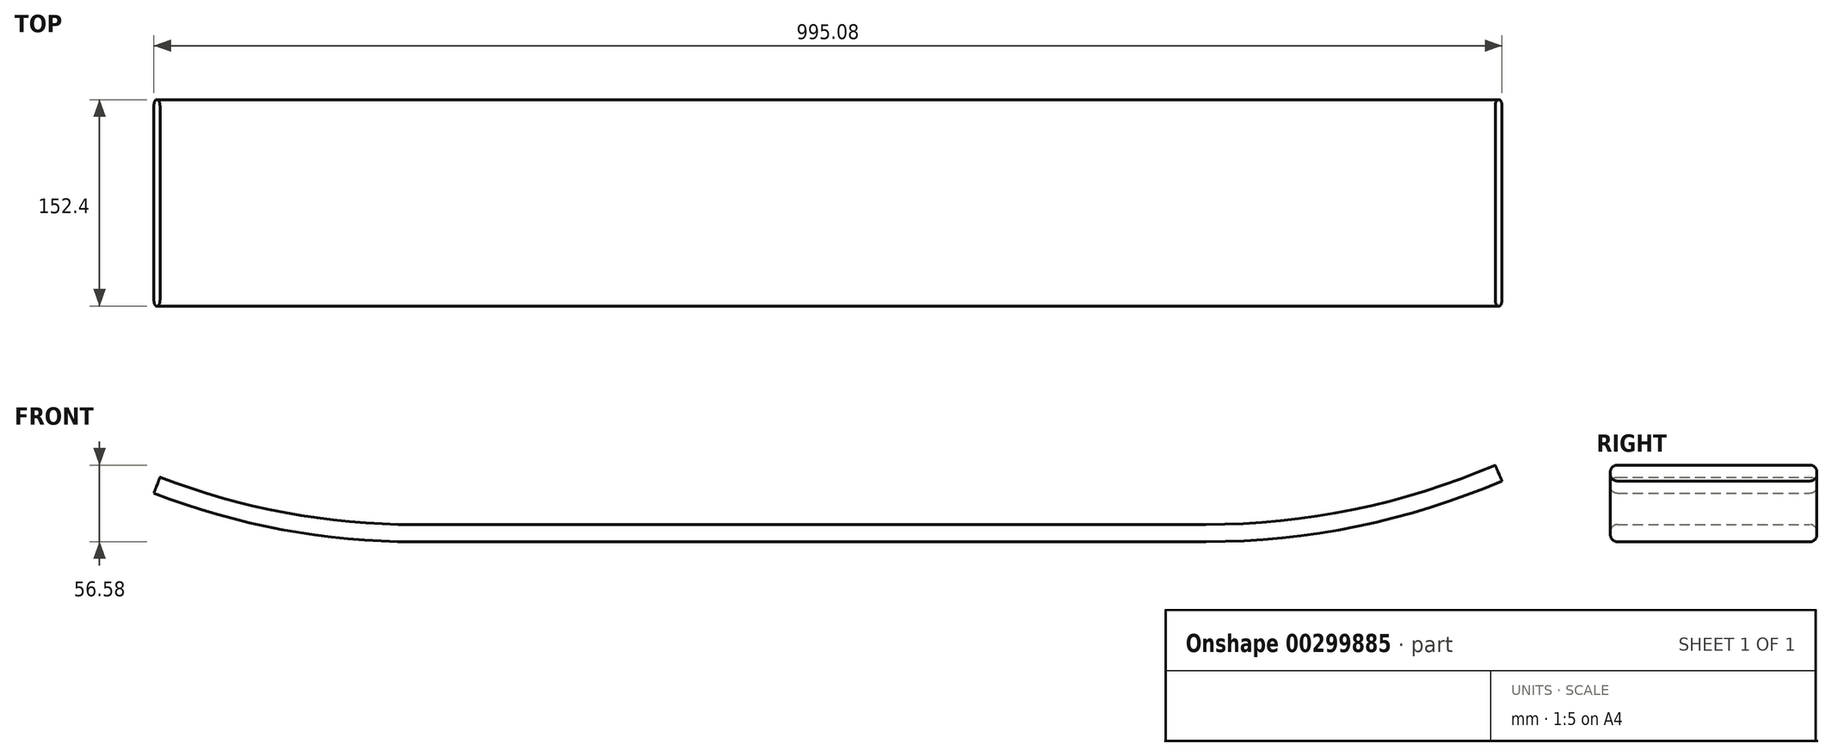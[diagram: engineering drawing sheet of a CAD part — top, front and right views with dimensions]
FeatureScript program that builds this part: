
annotation { "Feature Type Name" : "Feature", "Feature Type Description" : "" }
export const myFeature = defineFeature(function(context is Context, id is Id, definition is map)
    precondition{}
    {
        {
            var Q0;
            Q0=qCreatedBy(makeId("Front.planeOp"),FACE);
            var sketch = newSketch(context, id + "F0", { "sketchPlane" : qUnion([Q0])});
            skLineSegment(sketch, "E0", {"start": v(0, 0) * mm, "end": v(584.2, 0) * mm});
            skLineSegment(sketch, "E1.0", {"start": v(0, 12.7) * mm, "end": v(584.2, 12.7) * mm});
            skArc(sketch, "E2", {"start": v(-192.46, 35.86) * mm, "mid": v(-97.89, 9.04) * mm, "end": v(0, 0) * mm});
            skArc(sketch, "E3.0", {"start": v(-187.89, 47.7) * mm, "mid": v(-95.56, 21.53) * mm, "end": v(0, 12.7) * mm});
            skLineSegment(sketch, "E4", {"start": v(-192.46, 35.86) * mm, "end": v(-187.89, 47.7) * mm});
            skArc(sketch, "E5", {"start": v(584.2, 0) * mm, "mid": v(695.7, 11.34) * mm, "end": v(802.62, 44.91) * mm});
            skArc(sketch, "E6.0", {"start": v(584.2, 12.7) * mm, "mid": v(693.14, 23.78) * mm, "end": v(797.61, 56.58) * mm});
            skLineSegment(sketch, "E7", {"start": v(802.62, 44.91) * mm, "end": v(797.61, 56.58) * mm});
            skSolve(sketch);
        }
        {
            var Q0;
            Q0=makeQuery(id+"F0.imprint","IMPRINT",FACE,{"disambiguationData":[TD([[makeQuery(id+"F0.imprint","IMPRINT",EDGE,{"derivedFrom":sQuery(id+"F0.wireOp",EDGE,"E0")}),1.0]])]});
            extrude(context, id + "F1", {"entities" : qUnion([Q0]), "endBound" : BoundingType.SYMMETRIC, "depth" : 152.4 * mm});
        }
        {
            var Q0;
            Q0=makeQuery(id+"F1.opExtrude","CAP_EDGE",EDGE,{"disambiguationData":[OSD([sQuery(id+"F0.wireOp",EDGE,"E0")])],"isStart":true});
            var Q1;
            Q1=makeQuery(id+"F1.opExtrude","CAP_EDGE",EDGE,{"disambiguationData":[OSD([sQuery(id+"F0.wireOp",EDGE,"E1.0")])],"isStart":true});
            fillet(context, id + "F2", {"entities" : qUnion([Q0, Q1]), "radius" : 5.08 * mm, "tangentPropagation" : true, "allowEdgeOverflow" : false});
        }
        {
            var Q0;
            Q0=makeQuery(id+"F1.opExtrude","CAP_EDGE",EDGE,{"disambiguationData":[OSD([sQuery(id+"F0.wireOp",EDGE,"E0")])],"isStart":false});
            var Q1;
            Q1=makeQuery(id+"F1.opExtrude","CAP_EDGE",EDGE,{"disambiguationData":[OSD([sQuery(id+"F0.wireOp",EDGE,"E1.0")])],"isStart":false});
            fillet(context, id + "F3", {"entities" : qUnion([Q0, Q1]), "radius" : 5.08 * mm, "tangentPropagation" : true, "allowEdgeOverflow" : false});
        }
    });
